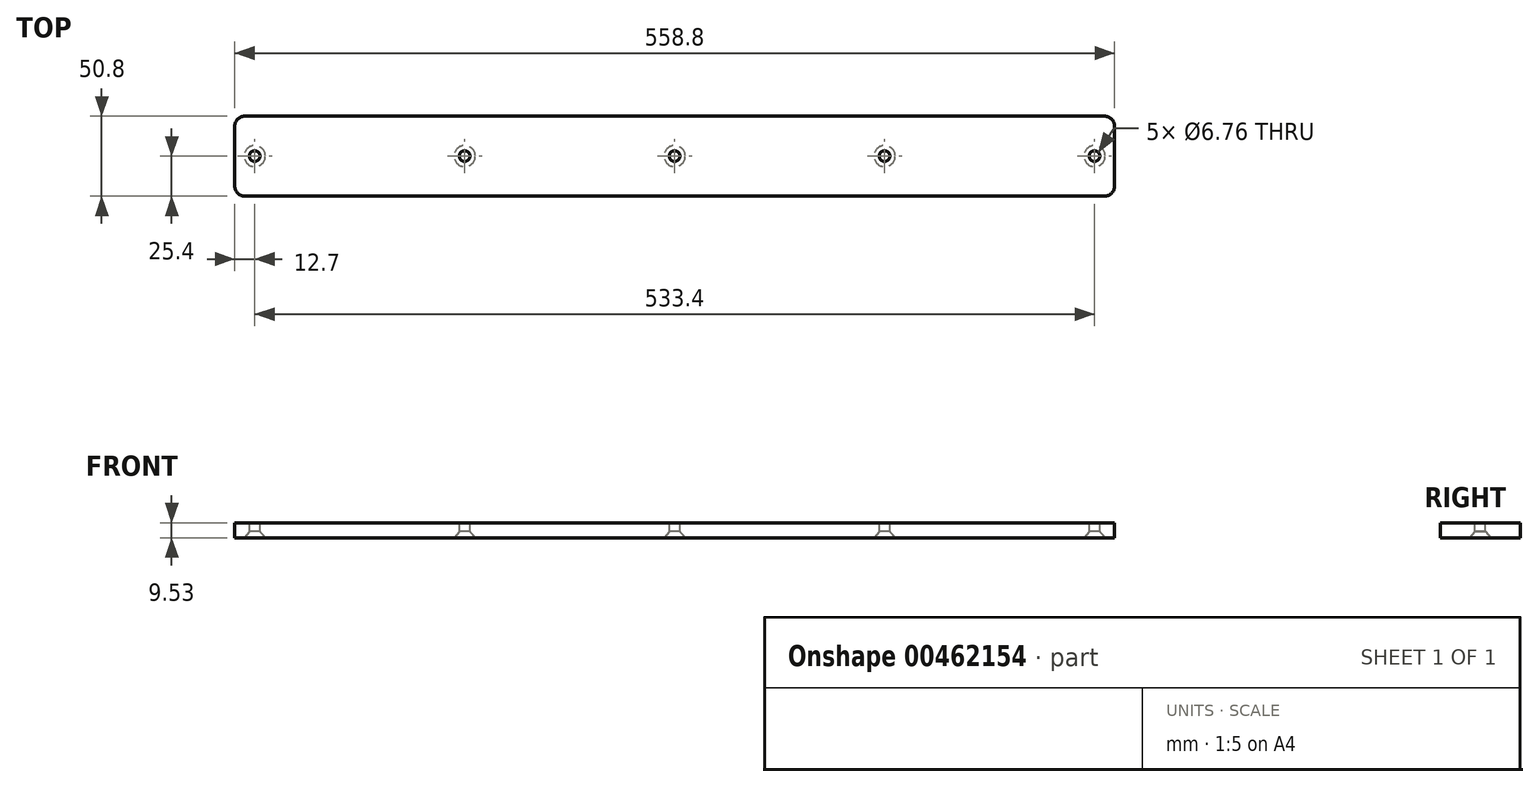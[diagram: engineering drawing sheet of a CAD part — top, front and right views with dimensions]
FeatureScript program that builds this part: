
annotation { "Feature Type Name" : "Feature", "Feature Type Description" : "" }
export const myFeature = defineFeature(function(context is Context, id is Id, definition is map)
    precondition{}
    {
        {
            var Q0;
            Q0=qCreatedBy(makeId("Top.planeOp"),FACE);
            var sketch = newSketch(context, id + "F0", { "sketchPlane" : qUnion([Q0])});
            skLineSegment(sketch, "E0.bottom", {"start": v(273.05, -25.4) * mm, "end": v(-273.05, -25.4) * mm});
            skLineSegment(sketch, "E0.top", {"start": v(273.05, 25.4) * mm, "end": v(-273.05, 25.4) * mm});
            skLineSegment(sketch, "E0.left", {"start": v(279.4, -19.05) * mm, "end": v(279.4, 19.05) * mm});
            skLineSegment(sketch, "E0.right", {"start": v(-279.4, -19.05) * mm, "end": v(-279.4, 19.05) * mm});
            skPoint(sketch, "E0.middle", {"position": v(0, 0) * mm});
            skPoint(sketch, "E1.visualSharp", {"position": v(-279.4, 25.4) * mm});
            skArc(sketch, "E1.filletArc", {"start": v(-273.05, 25.4) * mm, "mid": v(-277.54, 23.54) * mm, "end": v(-279.4, 19.05) * mm});
            skPoint(sketch, "E2.visualSharp", {"position": v(-279.4, -25.4) * mm});
            skArc(sketch, "E2.filletArc", {"start": v(-279.4, -19.05) * mm, "mid": v(-277.54, -23.54) * mm, "end": v(-273.05, -25.4) * mm});
            skPoint(sketch, "E3.visualSharp", {"position": v(279.4, 25.4) * mm});
            skArc(sketch, "E3.filletArc", {"start": v(279.4, 19.05) * mm, "mid": v(277.54, 23.54) * mm, "end": v(273.05, 25.4) * mm});
            skPoint(sketch, "E4.visualSharp", {"position": v(279.4, -25.4) * mm});
            skArc(sketch, "E4.filletArc", {"start": v(273.05, -25.4) * mm, "mid": v(277.54, -23.54) * mm, "end": v(279.4, -19.05) * mm});
            skLineSegment(sketch, "E5", {"start": v(279.4, 0) * mm, "end": v(-279.4, 0) * mm, "construction": true});
            skPoint(sketch, "E6", {"position": v(-266.7, 0) * mm});
            skPoint(sketch, "E7", {"position": v(-133.35, 0) * mm});
            skPoint(sketch, "E8", {"position": v(133.35, 0) * mm});
            skPoint(sketch, "E9", {"position": v(266.7, 0) * mm});
            skSolve(sketch);
        }
        {
            var Q0;
            Q0=makeQuery(id+"F0.imprint","IMPRINT",FACE,{"disambiguationData":[TD([[makeQuery(id+"F0.imprint","IMPRINT",EDGE,{"derivedFrom":sQuery(id+"F0.wireOp",EDGE,"E0.bottom")}),-1.0]])]});
            extrude(context, id + "F1", {"entities" : qUnion([Q0]), "depth" : 9.52 * mm});
        }
        {
            var Q0;
            Q0=sQuery(id+"F0.wireOp",VERTEX,"E9");
            var Q1;
            Q1=sQuery(id+"F0.wireOp",VERTEX,"E8");
            var Q2;
            Q2=sQuery(id+"F0.wireOp",VERTEX,"E0.middle");
            var Q3;
            Q3=sQuery(id+"F0.wireOp",VERTEX,"E7");
            var Q4;
            Q4=sQuery(id+"F0.wireOp",VERTEX,"E6");
            var Q5;
            Q5=makeQuery(id+"F1.opExtrude","SWEPT_BODY",BODY,{"disambiguationData":[OSD([sQuery(id+"F0.wireOp",EDGE,"E0.bottom"),sQuery(id+"F0.wireOp",EDGE,"E0.top"),sQuery(id+"F0.wireOp",EDGE,"E0.left"),sQuery(id+"F0.wireOp",EDGE,"E0.right"),sQuery(id+"F0.wireOp",EDGE,"E1.filletArc"),sQuery(id+"F0.wireOp",EDGE,"E2.filletArc"),sQuery(id+"F0.wireOp",EDGE,"E3.filletArc"),sQuery(id+"F0.wireOp",EDGE,"E4.filletArc")])]});
            hole(context, id + "F2", {"style" : HoleStyle.C_SINK, "endStyle" : HoleEndStyle.THROUGH, "oppositeDirection" : true, "standardTappedOrClearance" : lookupTablePath({ "standard" : "ANSI", "fit" : "Normal (ASME)", "size" : "1/4", "type" : "Clearance" }), "standardBlindInLast" : lookupTablePath({ "fit" : "Free", "standard" : "ANSI", "size" : "1/4", "type" : "Clearance" }), "holeDiameter" : 6.76 * mm, "cSinkDiameter" : 13.5 * mm, "cSinkAngle" : 82 * degree, "isTappedThrough" : true, "tappedDepth" : 57.15 * mm, "tapClearance" : 3, "locations" : qUnion([Q0, Q1, Q2, Q3, Q4]), "scope" : qUnion([Q5]), "startStyle" : HoleStartStyle.SKETCH});
        }
    });
